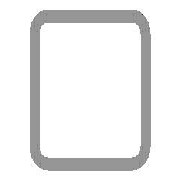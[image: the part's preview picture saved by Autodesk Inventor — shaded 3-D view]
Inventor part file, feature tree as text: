
AUTODESK INVENTOR PART (.ipt)
format: ipt  version: 2025.1 (Build 291241020, 241B)  size: 148,480 bytes
history: native  units: mm (DEFAULTED — no unit token found)
features: other x4, plane x3, split x2, sketch x1
ambient origin geometry x8: Origin, YZ Plane, XZ Plane, XY Plane, X Axis, Y Axis, Z Axis, Center Point
bodies: Solid1 (feature_tree), Body (feature_tree)
feature tree (10):
  parser-record x1  (decoder bookkeeping rows leaked as tree rows — omitted from the tree; the rows remain in map.json)
  other  "Driven Length"
  other  "Start Plane"
  other  "End Plane"
  plane  "Work Plane4"
  split  "Split1"
  plane  "Work Plane5"
  split  "Split2"
  sketch  "Sketch3"  dims[d3=565.685425mm d4=0.0mm d7=4.0mm d9=40.0mm d11=40.0mm d12=2.0mm d13=141.421356mm d14=707.106781mm d15=20.0mm d16=20.0mm d17=90.0deg d18=565.685425mm]
  plane  "Work Plane3"
